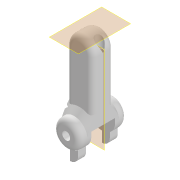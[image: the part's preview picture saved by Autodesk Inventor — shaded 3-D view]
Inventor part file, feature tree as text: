
AUTODESK INVENTOR PART (.ipt)
format: ipt  version: 2020.2 (Build 242310000, 310)  size: 272,896 bytes
history: native  units: mm
features: sketch x9, extrude x6, plane x2, mirror x2, fillet x2, chamfer x1, sweep x1
ambient origin geometry x8: Origin, YZ Plane, XZ Plane, XY Plane, X Axis, Y Axis, Z Axis, Center Point
bodies: Solid1 (feature_tree)
feature tree (23):
  extrude  "base"  Depth=10.0mm
  extrude  "joint"  Depth=25.0mm
  plane  "Work Plane1"
  mirror  "Mirror1"
  chamfer  "Chamfer1"  Distance=8.0mm
  fillet  "Fillet1"  Radius=3.0mm
  extrude  "joint_2"  Depth=5.0mm TaperAngle=0.0deg
  extrude  "lock"  Depth=2.0mm
  mirror  "Mirror2"
  fillet  "Fillet2"  Radius=10.5mm
  sweep  "Sweep2"
  extrude  "Extrusion8"  Depth=3.5mm
  plane  "Work Plane3"
  extrude  "Extrusion9"  Depth=2.5mm
  sketch  "Sketch1"  dims[d0=3.0mm d1=10.0mm]
  sketch  "Sketch2"  dims[d2=25.0mm d3=3.0mm]
  sketch  "Sketch3"  dims[d4=10.0mm d5=8.0mm d6=0.0mm d7=3.0mm]
  sketch  "Sketch9"  dims[d8=10.0mm d9=5.0mm d10=0.0mm]
  sketch  "Sketch10"  dims[d11=2.0mm d12=2.0mm d13=45.0deg d14=2.0mm d15=10.5mm]
  sketch  "Sketch11"  dims[d16=9.0mm d17=0.0mm d21=10.0mm]
  sketch  "Sketch12"  dims[d22=5.25mm d42=3.5mm]
  sketch  "Sketch13"  dims[d43=3.5mm d44=2.5mm]
  sketch  "Sketch14"  dims[d46=25.0mm d47=0.0mm d48=6.0mm d49=3.0mm d50=3.0mm d51=3.0mm d52=0.0mm d53=3.0mm d54=3.0mm d55=7.0mm d57=3.0mm d58=2.0mm d59=2.5mm d60=0.0mm d61=0.0mm d62=4.0mm d63=0.0mm d64=3.5mm d65=3.0mm d66=5.0mm d67=0.0mm]
